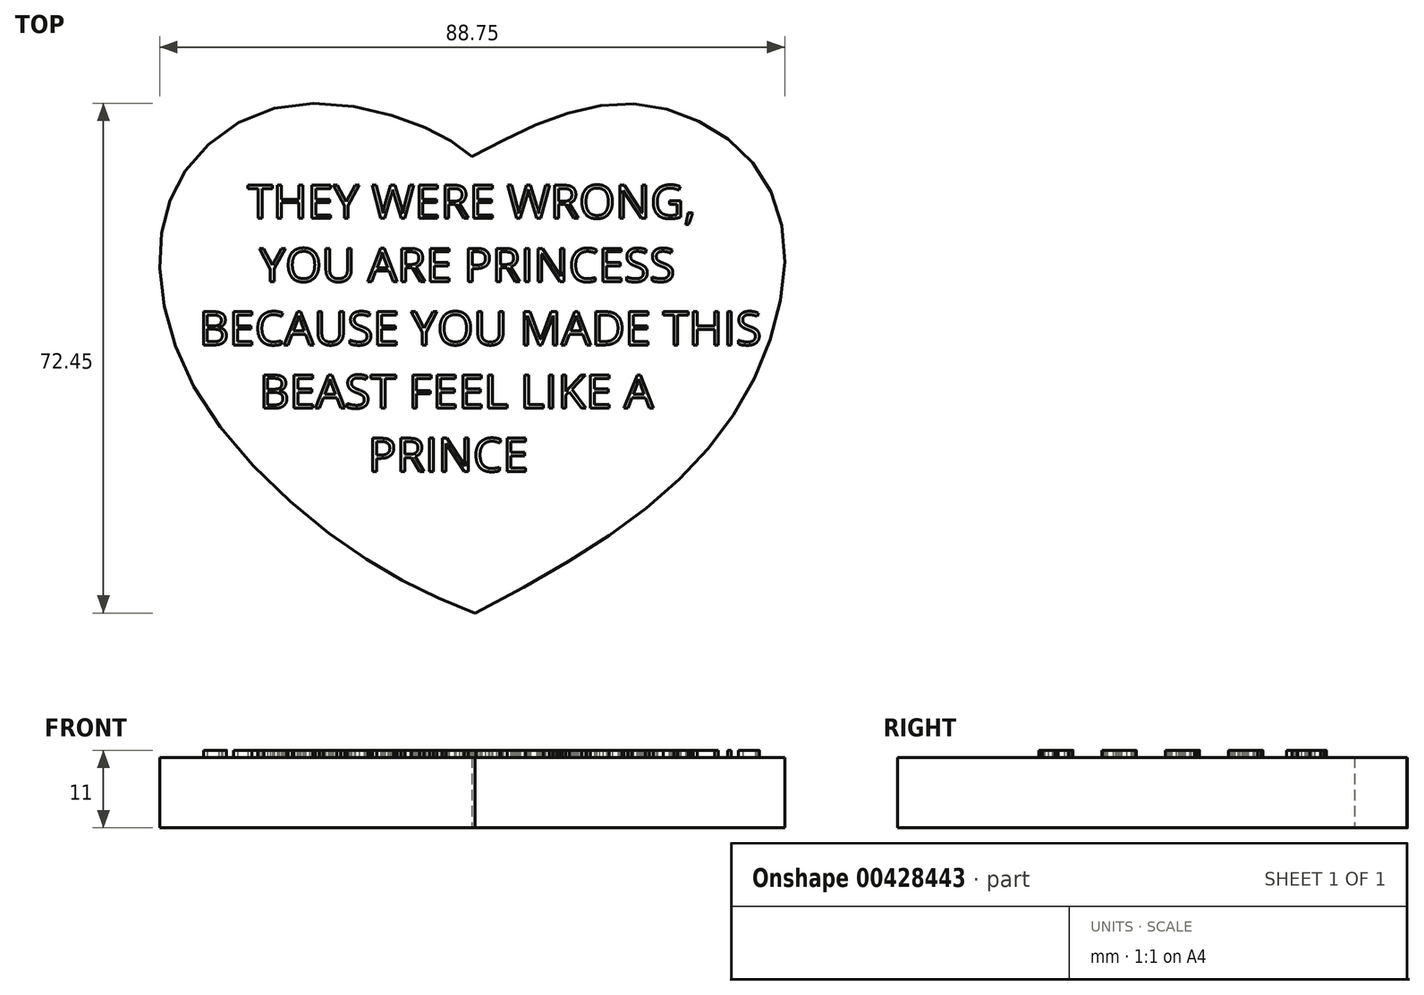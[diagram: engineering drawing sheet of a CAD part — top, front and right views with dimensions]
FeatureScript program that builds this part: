
annotation { "Feature Type Name" : "Feature", "Feature Type Description" : "" }
export const myFeature = defineFeature(function(context is Context, id is Id, definition is map)
    precondition{}
    {
        {
            var Q0;
            Q0=qCreatedBy(makeId("Top.planeOp"),FACE);
            var sketch = newSketch(context, id + "F0", { "sketchPlane" : qUnion([Q0])});
            skFitSpline(sketch, "E0", {"points": [v(49.6, 70.34) * mm, v(73.34, 77.72) * mm, v(92.4, 64.64) * mm, v(87.02, 34) * mm, v(50.07, 5.42) * mm], "startDerivative": vector(104.52, 55.2) * mm, "endDerivative": vector(-164.24, -85.38) * mm});
            skFitSpline(sketch, "E1", {"points": [v(49.6, 70.34) * mm, v(40.98, 75.22) * mm, v(22.79, 77.45) * mm, v(9.23, 68.72) * mm, v(5.28, 55.8) * mm, v(10.9, 36.23) * mm, v(31.88, 14.89) * mm, v(50.07, 5.42) * mm], "startDerivative": vector(-61.26, 53.1) * mm, "endDerivative": vector(123.7, -48.3) * mm});
            skSolve(sketch);
        }
        {
            var Q0;
            Q0=qCreatedBy(makeId("Top.planeOp"),FACE);
            var sketch = newSketch(context, id + "F1", { "sketchPlane" : qUnion([Q0])});
            skText(sketch, "E2", { "text": "    THEY WERE WRONG,\n     YOU ARE PRINCESS\nBECAUSE YOU MADE THIS \n     BEAST FEEL LIKE A \n              PRINCE", "fontName": "OpenSans-Regular.ttf"});
            const initialGuessF1  = {"E2": [0.01083, 0.06152, 1, 0, 0.00476]};
            skSetInitialGuess(sketch, initialGuessF1);
            skSolve(sketch);
        }
        {
            var Q0;
            Q0=makeQuery(id+"F0.imprint","IMPRINT",FACE,{"disambiguationData":[TD([[makeQuery(id+"F0.imprint","IMPRINT",EDGE,{"derivedFrom":sQuery(id+"F0.wireOp",EDGE,"E0")}),-1.0]])]});
            extrude(context, id + "F2", {"entities" : qUnion([Q0]), "endBound" : BoundingType.SYMMETRIC, "depth" : 10 * mm});
        }
        {
            var Q0;
            Q0 = qSketchRegion(id + "F1", true);
            extrude(context, id + "F3", {"entities" : qUnion([Q0]), "operationType" : NewBodyOperationType.ADD, "depth" : 6 * mm});
        }
    });
